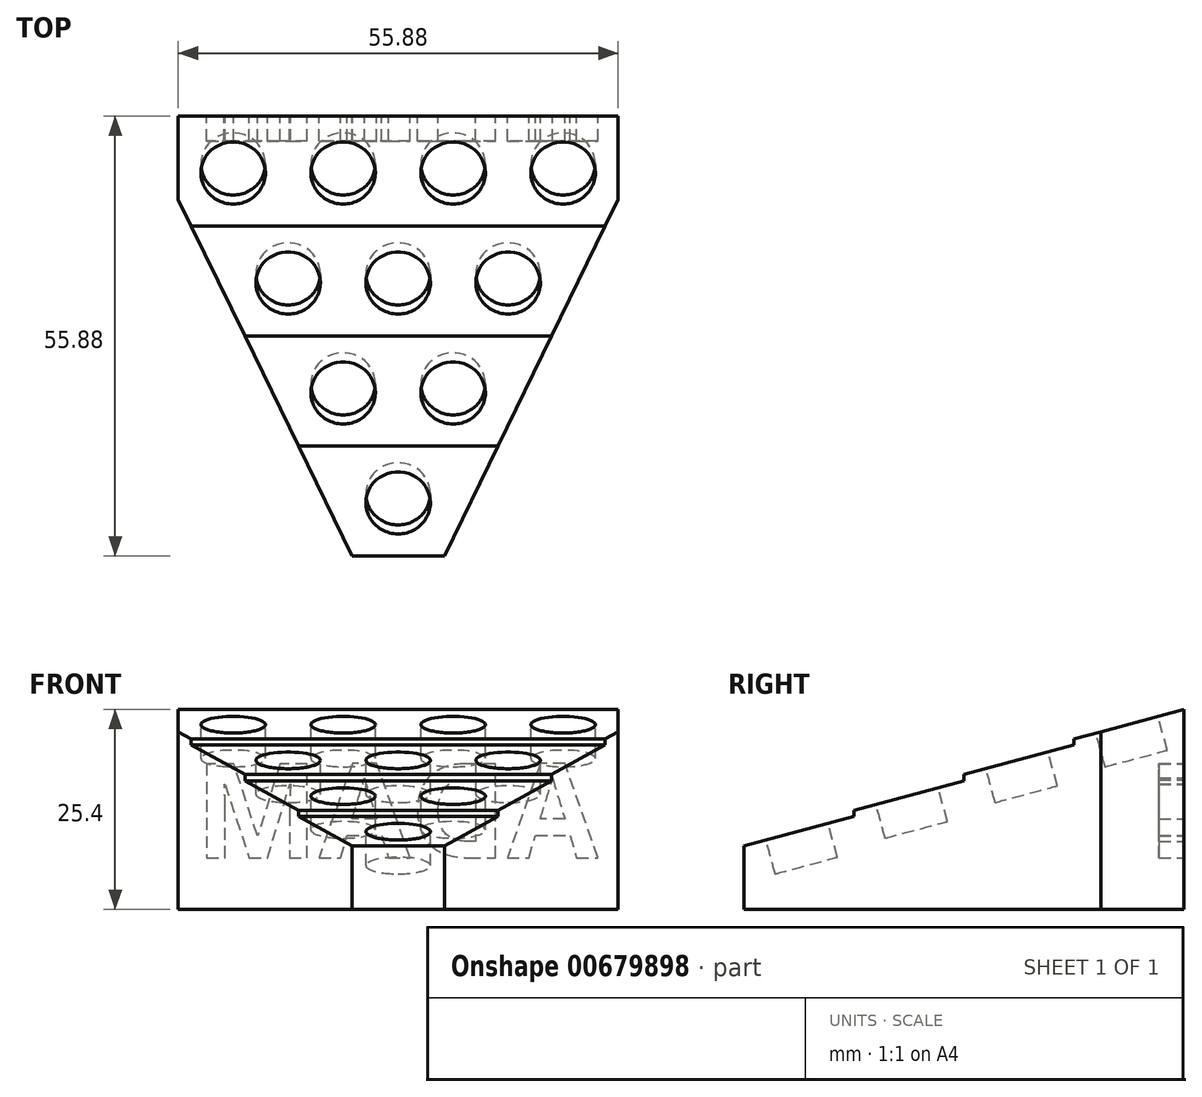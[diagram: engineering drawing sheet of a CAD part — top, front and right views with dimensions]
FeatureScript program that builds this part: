
annotation { "Feature Type Name" : "Feature", "Feature Type Description" : "" }
export const myFeature = defineFeature(function(context is Context, id is Id, definition is map)
    precondition{}
    {
        {
            var Q0;
            Q0=qCreatedBy(makeId("Top.planeOp"),FACE);
            var sketch = newSketch(context, id + "F0", { "sketchPlane" : qUnion([Q0])});
            skLineSegment(sketch, "E0.bottom", {"start": v(0, 0) * mm, "end": v(55.88, 0) * mm});
            skLineSegment(sketch, "E0.top", {"start": v(0, 55.88) * mm, "end": v(55.88, 55.88) * mm});
            skLineSegment(sketch, "E0.left", {"start": v(0, 0) * mm, "end": v(0, 55.88) * mm});
            skLineSegment(sketch, "E0.right", {"start": v(55.88, 0) * mm, "end": v(55.88, 55.88) * mm});
            skSolve(sketch);
        }
        {
            var Q0;
            Q0 = qSketchRegion(id + "F0", true);
            extrude(context, id + "F1", {"entities" : qUnion([Q0]), "depth" : 25.4 * mm, "offsetDistance" : 25.4 * mm});
        }
        {
            var Q0;
            Q0=makeQuery(id+"F1.opExtrude","SWEPT_FACE",FACE,{"disambiguationData":[OSD([sQuery(id+"F0.wireOp",EDGE,"E0.left")])]});
            var sketch = newSketch(context, id + "F2", { "sketchPlane" : qUnion([Q0])});
            skLineSegment(sketch, "E1", {"start": v(-55.88, 25.4) * mm, "end": v(-41.91, 21.66) * mm});
            skLineSegment(sketch, "E2", {"start": v(-41.91, 21.66) * mm, "end": v(-41.91, 20.87) * mm});
            skLineSegment(sketch, "E3", {"start": v(-27.94, 16.34) * mm, "end": v(-27.94, 17.12) * mm});
            skLineSegment(sketch, "E4", {"start": v(-13.97, 11.8) * mm, "end": v(-13.97, 12.6) * mm});
            skLineSegment(sketch, "E5", {"start": v(-41.91, 20.87) * mm, "end": v(-27.94, 17.12) * mm});
            skLineSegment(sketch, "E6", {"start": v(-27.94, 16.34) * mm, "end": v(-13.97, 12.6) * mm});
            skLineSegment(sketch, "E7", {"start": v(-13.97, 11.8) * mm, "end": v(0, 8.06) * mm});
            skLineSegment(sketch, "E8", {"start": v(-55.88, 25.4) * mm, "end": v(0, 25.4) * mm});
            skLineSegment(sketch, "E9", {"start": v(0, 25.4) * mm, "end": v(0, 8.06) * mm});
            skSolve(sketch);
        }
        {
            var Q0;
            Q0=makeQuery(id+"F2.imprint","IMPRINT",FACE,{"disambiguationData":[TD([[makeQuery(id+"F2.imprint","IMPRINT",EDGE,{"derivedFrom":sQuery(id+"F2.wireOp",EDGE,"E1")}),1.0]])]});
            extrude(context, id + "F3", {"entities" : qUnion([Q0]), "operationType" : NewBodyOperationType.REMOVE, "oppositeDirection" : true, "depth" : 76.2 * mm, "offsetDistance" : 25.4 * mm});
        }
        {
            var Q0;
            Q0=makeQuery(id+"F3.boolean.opBoolean","COPY",FACE,{"derivedFrom":makeQuery(id+"F3.opExtrude","SWEPT_FACE",FACE,{"disambiguationData":[OSD([sQuery(id+"F2.wireOp",EDGE,"E1")])]})});
            var sketch = newSketch(context, id + "F4", { "sketchPlane" : qUnion([Q0])});
            skCircle(sketch, "E10", {"center": v(20.96, 53.07) * mm, "radius": 4.09 * mm});
            skCircle(sketch, "E11.1.0.0", {"center": v(34.93, 53.07) * mm, "radius": 4.09 * mm});
            skLineSegment(sketch, "E11.direction1", {"start": v(20.96, 53.07) * mm, "end": v(34.93, 53.07) * mm, "construction": true});
            skLineSegment(sketch, "E12", {"start": v(27.94, 60.55) * mm, "end": v(27.94, 0) * mm});
            skCircle(sketch, "E13.1.0.0", {"center": v(6.98, 53.07) * mm, "radius": 4.09 * mm});
            skLineSegment(sketch, "E13.direction1", {"start": v(20.96, 53.07) * mm, "end": v(6.98, 53.07) * mm, "construction": true});
            skCircle(sketch, "E14.1.0.0", {"center": v(48.9, 53.07) * mm, "radius": 4.09 * mm});
            skLineSegment(sketch, "E14.direction1", {"start": v(34.93, 53.07) * mm, "end": v(48.9, 53.07) * mm, "construction": true});
            skSolve(sketch);
        }
        {
            var Q0;
            Q0 = qSketchRegion(id + "F4", true);
            extrude(context, id + "F5", {"entities" : qUnion([Q0]), "operationType" : NewBodyOperationType.REMOVE, "oppositeDirection" : true, "depth" : 4.44 * mm, "offsetDistance" : 25.4 * mm});
        }
        {
            var Q0;
            Q0=makeQuery(id+"F3.boolean.opBoolean","COPY",FACE,{"derivedFrom":makeQuery(id+"F3.opExtrude","SWEPT_FACE",FACE,{"disambiguationData":[OSD([sQuery(id+"F2.wireOp",EDGE,"E5")])]})});
            var sketch = newSketch(context, id + "F6", { "sketchPlane" : qUnion([Q0])});
            skLineSegment(sketch, "E15", {"start": v(27.94, 60.72) * mm, "end": v(27.94, -9.02) * mm});
            skCircle(sketch, "E16", {"center": v(27.94, 38.4) * mm, "radius": 4.09 * mm});
            skCircle(sketch, "E17.1.0.0", {"center": v(41.91, 38.4) * mm, "radius": 4.09 * mm});
            skLineSegment(sketch, "E17.direction1", {"start": v(27.94, 38.4) * mm, "end": v(41.91, 38.4) * mm, "construction": true});
            skCircle(sketch, "E18.1.0.0", {"center": v(13.97, 38.4) * mm, "radius": 4.09 * mm});
            skLineSegment(sketch, "E18.direction1", {"start": v(27.94, 38.4) * mm, "end": v(13.97, 38.4) * mm, "construction": true});
            skSolve(sketch);
        }
        {
            var Q0;
            Q0 = qSketchRegion(id + "F6", true);
            extrude(context, id + "F7", {"entities" : qUnion([Q0]), "operationType" : NewBodyOperationType.REMOVE, "oppositeDirection" : true, "depth" : 4.44 * mm, "offsetDistance" : 25.4 * mm});
        }
        {
            var Q0;
            Q0=makeQuery(id+"F3.boolean.opBoolean","COPY",FACE,{"derivedFrom":makeQuery(id+"F3.opExtrude","SWEPT_FACE",FACE,{"disambiguationData":[OSD([sQuery(id+"F2.wireOp",EDGE,"E6")])]})});
            var sketch = newSketch(context, id + "F8", { "sketchPlane" : qUnion([Q0])});
            skPoint(sketch, "E19.endSnap0", {"position": v(27.94, 16.75) * mm});
            skLineSegment(sketch, "E20", {"start": v(27.94, 66.34) * mm, "end": v(27.94, -7.4) * mm});
            skCircle(sketch, "E21", {"center": v(20.96, 23.74) * mm, "radius": 4.09 * mm});
            skCircle(sketch, "E22.MirrorC", {"center": v(34.93, 23.74) * mm, "radius": 4.09 * mm});
            skSolve(sketch);
        }
        {
            var Q0;
            Q0 = qSketchRegion(id + "F8", true);
            extrude(context, id + "F9", {"entities" : qUnion([Q0]), "operationType" : NewBodyOperationType.REMOVE, "oppositeDirection" : true, "depth" : 4.44 * mm, "offsetDistance" : 25.4 * mm});
        }
        {
            var Q0;
            Q0=makeQuery(id+"F3.boolean.opBoolean","COPY",FACE,{"derivedFrom":makeQuery(id+"F3.opExtrude","SWEPT_FACE",FACE,{"disambiguationData":[OSD([sQuery(id+"F2.wireOp",EDGE,"E7")])]})});
            var sketch = newSketch(context, id + "F10", { "sketchPlane" : qUnion([Q0])});
            skLineSegment(sketch, "E23", {"start": v(27.94, 60.75) * mm, "end": v(27.94, -5.43) * mm});
            skCircle(sketch, "E24", {"center": v(27.94, 9.07) * mm, "radius": 4.09 * mm});
            skSolve(sketch);
        }
        {
            var Q0;
            Q0 = qSketchRegion(id + "F10", true);
            var Q1;
            Q1=sQuery(id+"F10.wireOp",EDGE,"E24");
            extrude(context, id + "F11", {"entities" : qUnion([Q0]), "operationType" : NewBodyOperationType.REMOVE, "surfaceEntities" : qUnion([Q1]), "oppositeDirection" : true, "depth" : 4.44 * mm, "offsetDistance" : 25.4 * mm});
        }
        {
            var Q0;
            Q0=qCreatedBy(makeId("Top.planeOp"),FACE);
            var sketch = newSketch(context, id + "F12", { "sketchPlane" : qUnion([Q0])});
            skLineSegment(sketch, "E25", {"start": v(-1.1, 47.57) * mm, "end": v(27.15, -10.4) * mm});
            skLineSegment(sketch, "E26", {"start": v(27.94, 58.93) * mm, "end": v(27.94, -3.15) * mm, "construction": true});
            skLineSegment(sketch, "E27.MirrorCS", {"start": v(56.99, 47.57) * mm, "end": v(28.73, -10.4) * mm});
            skLineSegment(sketch, "E28", {"start": v(-1.1, 47.57) * mm, "end": v(-1.1, -10.4) * mm});
            skLineSegment(sketch, "E29", {"start": v(27.15, -10.4) * mm, "end": v(-1.1, -10.4) * mm});
            skLineSegment(sketch, "E30.MirrorCS", {"start": v(56.99, 47.57) * mm, "end": v(56.99, -10.4) * mm});
            skLineSegment(sketch, "E31.MirrorCS", {"start": v(28.73, -10.4) * mm, "end": v(56.99, -10.4) * mm});
            skSolve(sketch);
        }
        {
            var Q0;
            Q0 = qSketchRegion(id + "F12", true);
            extrude(context, id + "F13", {"entities" : qUnion([Q0]), "operationType" : NewBodyOperationType.REMOVE, "depth" : 25.4 * mm, "offsetDistance" : 25.4 * mm});
        }
        {
            var Q0;
            Q0=makeQuery(id+"F1.opExtrude","SWEPT_FACE",FACE,{"disambiguationData":[OSD([sQuery(id+"F0.wireOp",EDGE,"E0.top")])]});
            var sketch = newSketch(context, id + "F14", { "sketchPlane" : qUnion([Q0])});
            skText(sketch, "E32", { "text": "ADAM", "fontName": "OpenSans-Bold.ttf"});
            const initialGuessF14  = {"E32": [-0.05334, 0.00656, 1, 0, 0.01204]};
            skSetInitialGuess(sketch, initialGuessF14);
            skSolve(sketch);
        }
        {
            var Q0;
            Q0 = qSketchRegion(id + "F14", true);
            extrude(context, id + "F15", {"entities" : qUnion([Q0]), "operationType" : NewBodyOperationType.REMOVE, "oppositeDirection" : true, "depth" : 3.17 * mm, "offsetDistance" : 25.4 * mm});
        }
    });
